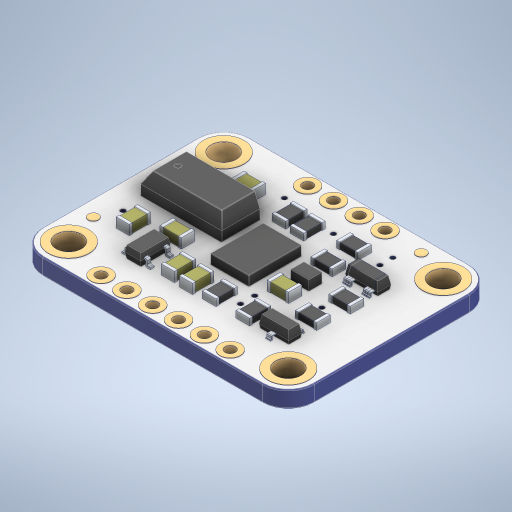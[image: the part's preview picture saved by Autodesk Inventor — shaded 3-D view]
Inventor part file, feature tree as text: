
AUTODESK INVENTOR PART (.ipt)
format: ipt  version: 2024.2 (Build 282272000, 272)  size: 953,344 bytes
history: native  units: in
note: dims shown in document units (in); Inventor stores cm internally (conversion verified against a paired STEP export)
features: other x71, mirror x19, fillet x2, chamfer x2
ambient origin geometry x8: Origin, YZ Plane, XZ Plane, XY Plane, X Axis, Y Axis, Z Axis, Center Point
bodies: Solid1 (feature_tree), Solid2 (feature_tree), Solid3 (feature_tree), Solid4 (feature_tree), Solid5 (feature_tree), Solid6 (feature_tree), Solid7 (feature_tree), Solid8 (feature_tree), Solid9 (feature_tree), Solid10 (feature_tree), Solid11 (feature_tree), Solid12 (feature_tree), Solid13 (feature_tree), Solid14 (feature_tree), Solid15 (feature_tree), Solid16 (feature_tree), Solid17 (feature_tree), Solid18 (feature_tree), Solid19 (feature_tree), Solid20 (feature_tree), Solid21 (feature_tree), Solid22 (feature_tree), Solid23 (feature_tree), Solid24 (feature_tree), Solid25 (feature_tree), Solid26 (feature_tree), Solid27 (feature_tree), Solid28 (feature_tree), Solid29 (feature_tree), Solid30 (feature_tree), Solid31 (feature_tree), Solid32 (feature_tree), Solid33 (feature_tree), Solid34 (feature_tree), Solid35 (feature_tree), Solid36 (feature_tree), Solid37 (feature_tree), Solid38 (feature_tree), Solid39 (feature_tree), Solid40 (feature_tree), Solid41 (feature_tree), Solid42 (feature_tree), Solid43 (feature_tree), Solid44 (feature_tree), Solid45 (feature_tree), Solid46 (feature_tree), Solid47 (feature_tree), Solid48 (feature_tree), Solid49 (feature_tree), Solid50 (feature_tree), Solid51 (feature_tree), Solid52 (feature_tree), Solid53 (feature_tree), Solid54 (feature_tree), Solid55 (feature_tree), Solid56 (feature_tree), Solid57 (feature_tree), Solid58 (feature_tree), Solid59 (feature_tree), Solid60 (feature_tree), Solid61 (feature_tree), Solid62 (feature_tree), Solid63 (feature_tree), Solid64 (feature_tree), Solid65 (feature_tree), Solid66 (feature_tree), Solid67 (feature_tree), Solid68 (feature_tree), Solid69 (feature_tree), Solid70 (feature_tree), Solid71 (feature_tree), Solid72 (feature_tree), Solid73 (feature_tree), Solid74 (feature_tree), Solid75 (feature_tree), Solid76 (feature_tree), Solid77 (feature_tree), Solid78 (feature_tree), Solid79 (feature_tree), Solid80 (feature_tree), Solid81 (feature_tree), Solid82 (feature_tree), Solid83 (feature_tree), Solid84 (feature_tree), Solid85 (feature_tree), Solid86 (feature_tree), Solid87 (feature_tree), Solid88 (feature_tree), Solid89 (feature_tree), Solid90 (feature_tree), Solid91 (feature_tree), Solid92 (feature_tree), Solid93 (feature_tree), Solid94 (feature_tree)
feature tree (94):
  fillet  "Fillet2"  [1 undecoded]
  other  "Boss-Extrude4[1]"
  other  "Boss-Extrude4[2]"
  other  "Boss-Extrude4[3]"
  other  "Boss-Extrude4[4]"
  other  "Boss-Extrude4[5]"
  other  "Boss-Extrude4[6]"
  other  "Boss-Extrude5[1]"
  other  "Boss-Extrude5[2]"
  other  "Boss-Extrude5[3]"
  other  "Boss-Extrude5[4]"
  other  "Boss-Extrude5[5]"
  other  "Boss-Extrude5[6]"
  other  "Boss-Extrude5[7]"
  other  "Boss-Extrude5[8]"
  chamfer  "Chamfer4"  [1 undecoded]
  other  "Boss-Extrude7[1]"
  other  "Boss-Extrude7[2]"
  other  "LPattern3[1]"
  other  "LPattern3[2]"
  other  "LPattern4"
  chamfer  "Chamfer6"  [1 undecoded]
  other  "Boss-Extrude9"
  other  "LPattern5"
  other  "LPattern6"
  mirror  "Mirror1"
  mirror  "Mirror2[1]"
  mirror  "Mirror2[2]"
  mirror  "Mirror2[3]"
  mirror  "Mirror2[4]"
  other  "LPattern9[1]"
  other  "LPattern9[2]"
  other  "LPattern9[3]"
  other  "LPattern9[4]"
  other  "Boss-Extrude10[1]"
  other  "Boss-Extrude10[2]"
  other  "Boss-Extrude10[3]"
  other  "Boss-Extrude10[4]"
  other  "Boss-Extrude10[5]"
  other  "Boss-Extrude10[6]"
  other  "Boss-Extrude10[7]"
  other  "Boss-Extrude10[8]"
  other  "Boss-Extrude10[9]"
  other  "Boss-Extrude10[10]"
  other  "Boss-Extrude10[11]"
  other  "Boss-Extrude10[12]"
  other  "Boss-Extrude10[13]"
  other  "Boss-Extrude10[14]"
  other  "Boss-Extrude10[15]"
  other  "Boss-Extrude10[16]"
  mirror  "Mirror3[1]"
  mirror  "Mirror3[2]"
  mirror  "Mirror3[3]"
  mirror  "Mirror3[4]"
  mirror  "Mirror3[5]"
  mirror  "Mirror3[6]"
  mirror  "Mirror3[7]"
  mirror  "Mirror3[8]"
  mirror  "Mirror3[9]"
  mirror  "Mirror3[10]"
  mirror  "Mirror3[11]"
  mirror  "Mirror3[12]"
  mirror  "Mirror3[13]"
  mirror  "Mirror3[14]"
  fillet  "Fillet10"  [1 undecoded]
  other  "Boss-Extrude11[1]"
  other  "Boss-Extrude11[2]"
  other  "Boss-Extrude11[3]"
  other  "Boss-Extrude11[4]"
  other  "Boss-Extrude11[5]"
  other  "Boss-Extrude11[6]"
  other  "Boss-Extrude11[7]"
  other  "Boss-Extrude11[8]"
  other  "Boss-Extrude11[9]"
  other  "Boss-Extrude11[10]"
  other  "Boss-Extrude11[11]"
  other  "Boss-Extrude11[12]"
  other  "Boss-Extrude11[13]"
  other  "Boss-Extrude11[14]"
  other  "Boss-Extrude11[15]"
  other  "Boss-Extrude11[16]"
  other  "Boss-Extrude12[1]"
  other  "Boss-Extrude12[2]"
  other  "Boss-Extrude12[3]"
  other  "Boss-Extrude12[4]"
  other  "Boss-Extrude12[5]"
  other  "Boss-Extrude12[6]"
  other  "Boss-Extrude12[7]"
  other  "Boss-Extrude12[8]"
  other  "Boss-Extrude12[9]"
  other  "Boss-Extrude12[10]"
  other  "Boss-Extrude12[11]"
  other  "Boss-Extrude12[12]"
  other  "Boss-Extrude13"
note: 4 required parameter values undecoded (feature->parameter linkage not recoverable at this tier; creation-order binding heuristic only, values carry confidence <= 0.55)
